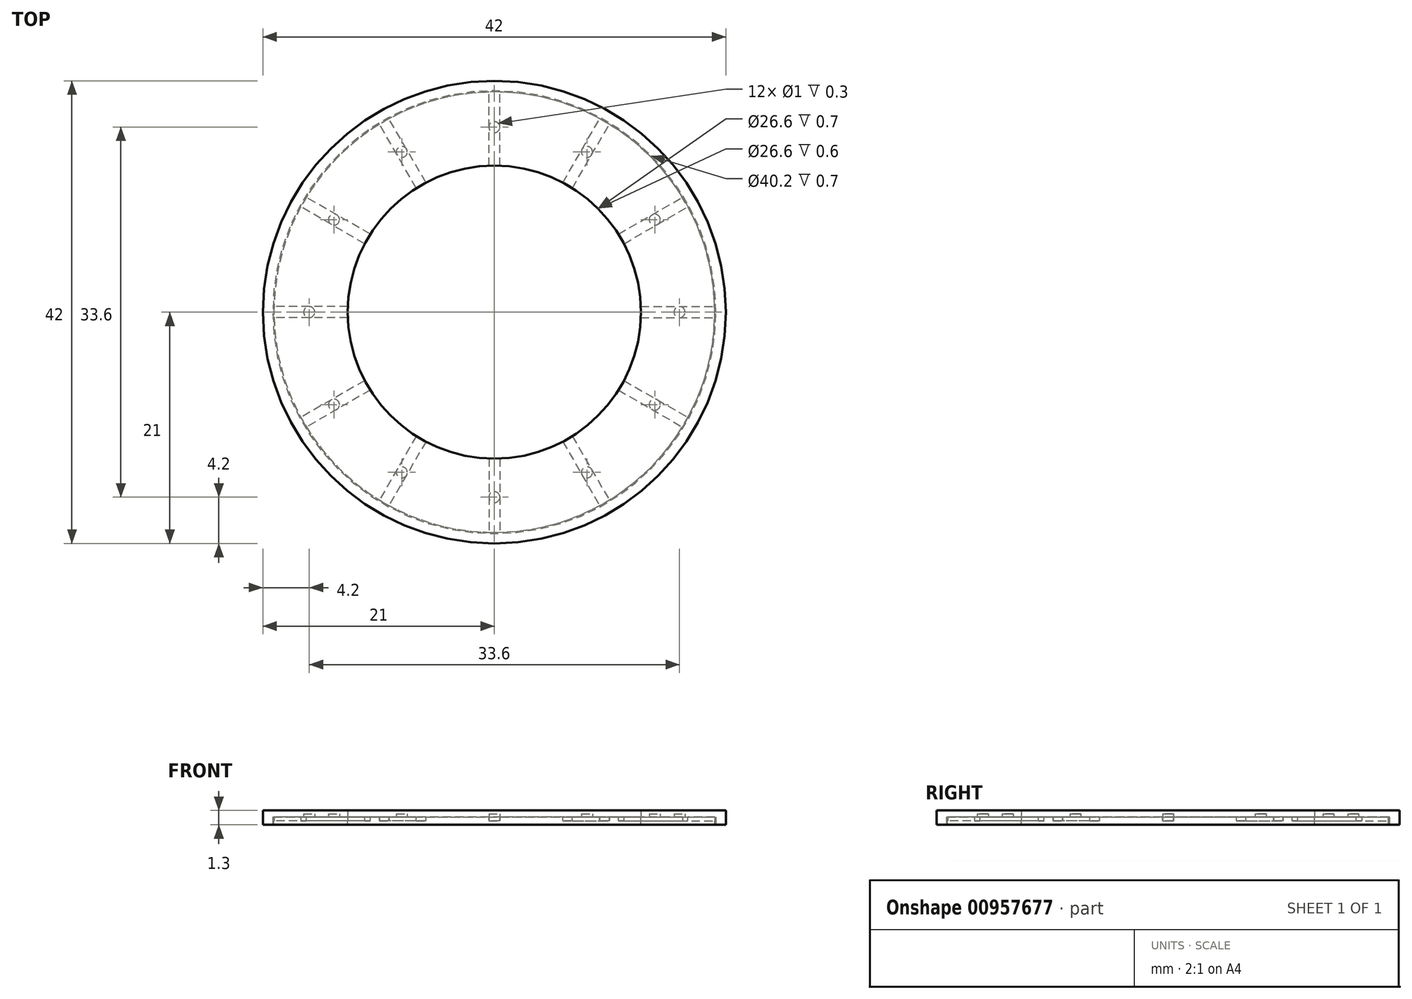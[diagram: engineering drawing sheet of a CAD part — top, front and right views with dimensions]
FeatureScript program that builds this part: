
annotation { "Feature Type Name" : "Feature", "Feature Type Description" : "" }
export const myFeature = defineFeature(function(context is Context, id is Id, definition is map)
    precondition{}
    {
        {
            var Q0;
            Q0=qCreatedBy(makeId("Top.planeOp"),FACE);
            var sketch = newSketch(context, id + "F0", { "sketchPlane" : qUnion([Q0])});
            skCircle(sketch, "E0", {"center": v(0, 0) * mm, "radius": 20 * mm});
            skCircle(sketch, "E1.0", {"center": v(0, 0) * mm, "radius": 13.3 * mm});
            skArc(sketch, "E2", {"start": v(0, 20) * mm, "mid": v(-3.35, 16.65) * mm, "end": v(0, 13.3) * mm});
            skLineSegment(sketch, "E3", {"start": v(0, 13.3) * mm, "end": v(0, 0) * mm, "construction": true});
            skLineSegment(sketch, "E4.1.0", {"start": v(-6.65, 11.52) * mm, "end": v(0, 0) * mm, "construction": true});
            skLineSegment(sketch, "E4.2.0", {"start": v(-11.52, 6.65) * mm, "end": v(0, 0) * mm, "construction": true});
            skLineSegment(sketch, "E5.1.3.0", {"start": v(-13.3, 0) * mm, "end": v(0, 0) * mm, "construction": true});
            skLineSegment(sketch, "E5.1.4.0", {"start": v(-11.52, -6.65) * mm, "end": v(0, 0) * mm, "construction": true});
            skLineSegment(sketch, "E5.1.5.0", {"start": v(-6.65, -11.52) * mm, "end": v(0, 0) * mm, "construction": true});
            skLineSegment(sketch, "E5.1.6.0", {"start": v(0, -13.3) * mm, "end": v(0, 0) * mm, "construction": true});
            skLineSegment(sketch, "E5.1.7.0", {"start": v(6.65, -11.52) * mm, "end": v(0, 0) * mm, "construction": true});
            skLineSegment(sketch, "E5.1.8.0", {"start": v(11.52, -6.65) * mm, "end": v(0, 0) * mm, "construction": true});
            skLineSegment(sketch, "E5.1.9.0", {"start": v(13.3, 0) * mm, "end": v(0, 0) * mm, "construction": true});
            skLineSegment(sketch, "E5.1.10.0", {"start": v(11.52, 6.65) * mm, "end": v(0, 0) * mm, "construction": true});
            skLineSegment(sketch, "E5.1.11.0", {"start": v(6.65, 11.52) * mm, "end": v(0, 0) * mm, "construction": true});
            skLineSegment(sketch, "E6", {"start": v(11.52, -6.65) * mm, "end": v(17.32, -10) * mm, "construction": true});
            skArc(sketch, "E7", {"start": v(17.32, -10) * mm, "mid": v(12.74, -11.23) * mm, "end": v(11.52, -6.65) * mm});
            skCircle(sketch, "E8.0", {"center": v(0, 0) * mm, "radius": 21 * mm});
            skSolve(sketch);
        }
        {
            var Q0;
            {var subQ1=sQuery(id+"F0.wireOp",EDGE,"E2");Q0=makeQuery(id+"F0.imprint","IMPRINT",FACE,{"disambiguationData":[TD([[makeQuery(id+"F0.imprint","IMPRINT",EDGE,{"derivedFrom":subQ1}),1.0]])]});}
            var Q1;
            Q1=makeQuery(id+"F0.imprint","IMPRINT",FACE,{"disambiguationData":[TD([[makeQuery(id+"F0.imprint","IMPRINT",EDGE,{"derivedFrom":sQuery(id+"F0.wireOp",EDGE,"Xude94sI-W2Tp-Iu3P-RemY-LlCTyh9PK2tk")}),1.0]])]});
            var Q2;
            Q2=makeQuery(id+"F0.imprint","IMPRINT",FACE,{"disambiguationData":[TD([[makeQuery(id+"F0.imprint","IMPRINT",EDGE,{"derivedFrom":sQuery(id+"F0.wireOp",EDGE,"zjPRt4QC-Xd3l-se5C-XvQx-mcNvj67eJI4K")}),-1.0]])]});
            extrude(context, id + "F1", {"entities" : qUnion([Q0, Q1, Q2]), "depth" : 0.2 * mm, "offsetDistance" : 25 * mm});
        }
        {
            var Q0;
            Q0=makeQuery(id+"F1.opExtrude","CAP_FACE",FACE,{"disambiguationData":[OSD([sQuery(id+"F0.wireOp",EDGE,"E0"),sQuery(id+"F0.wireOp",EDGE,"E1.0"),sQuery(id+"F0.wireOp",EDGE,"E2"),sQuery(id+"F0.wireOp",EDGE,"E7")])],"isStart":false});
            var sketch = newSketch(context, id + "F2", { "sketchPlane" : qUnion([Q0])});
            skCircle(sketch, "E9", {"center": v(0, 16.65) * mm, "radius": 0.5 * mm});
            skSolve(sketch);
        }
        {
            var Q0;
            Q0=makeQuery(id+"F0.imprint","IMPRINT",FACE,{"disambiguationData":[TD([[makeQuery(id+"F0.imprint","IMPRINT",EDGE,{"derivedFrom":sQuery(id+"F0.wireOp",EDGE,"zjPRt4QC-Xd3l-se5C-XvQx-mcNvj67eJI4K")}),1.0]])]});
            var Q1;
            Q1=makeQuery(id+"F2.imprint","IMPRINT",FACE,{"disambiguationData":[TD([[makeQuery(id+"F2.imprint","IMPRINT",EDGE,{"derivedFrom":sQuery(id+"F2.wireOp",EDGE,"E9")}),1.0]])]});
            extrude(context, id + "F3", {"entities" : qUnion([Q0, Q1]), "operationType" : NewBodyOperationType.ADD, "depth" : 0.3 * mm, "offsetDistance" : 25 * mm});
        }
        {
            var Q0;
            Q0=makeQuery(id+"F1.opExtrude","CAP_FACE",FACE,{"disambiguationData":[OSD([sQuery(id+"F0.wireOp",EDGE,"E0"),sQuery(id+"F0.wireOp",EDGE,"E1.0"),sQuery(id+"F0.wireOp",EDGE,"E2"),sQuery(id+"F0.wireOp",EDGE,"E7")])],"isStart":true});
            var sketch = newSketch(context, id + "F4", { "sketchPlane" : qUnion([Q0])});
            skCircle(sketch, "E10", {"center": v(16.02, 9.25) * mm, "radius": 0.5 * mm});
            skLineSegment(sketch, "E11", {"start": v(11.52, 6.65) * mm, "end": v(17.32, 10) * mm, "construction": true});
            skSolve(sketch);
        }
        {
            var Q0;
            Q0=makeQuery(id+"F4.imprint","IMPRINT",FACE,{"disambiguationData":[TD([[makeQuery(id+"F4.imprint","IMPRINT",EDGE,{"derivedFrom":sQuery(id+"F4.wireOp",EDGE,"E10")}),1.0]])]});
            extrude(context, id + "F5", {"entities" : qUnion([Q0]), "operationType" : NewBodyOperationType.ADD, "depth" : 0.3 * mm, "offsetDistance" : 25 * mm});
        }
        {
            var Q0;
            {var subQ0=sQuery(id+"F0.wireOp",EDGE,"E2");Q0=makeQuery(id+"F0.imprint","IMPRINT",FACE,{"disambiguationData":[TD([[makeQuery(id+"F0.imprint","IMPRINT",EDGE,{"derivedFrom":subQ0}),1.0]])]});}
            var Q1;
            {var subQ0=sQuery(id+"F0.wireOp",EDGE,"E2");Q1=makeQuery(id+"F0.imprint","IMPRINT",FACE,{"disambiguationData":[TD([[makeQuery(id+"F0.imprint","IMPRINT",EDGE,{"derivedFrom":subQ0}),-1.0]])]});}
            extrude(context, id + "F6", {"entities" : qUnion([Q0, Q1]), "depth" : 0.6 * mm, "offsetDistance" : 25 * mm});
        }
        {
            var Q0;
            Q0=makeQuery(id+"F0.imprint","IMPRINT",FACE,{"disambiguationData":[TD([[makeQuery(id+"F0.imprint","IMPRINT",EDGE,{"derivedFrom":sQuery(id+"F0.wireOp",EDGE,"E8.0")}),1.0]])]});
            var Q1;
            Q1=sQuery(id+"F0.wireOp",EDGE,"E8.0");
            var Q2;
            Q2=makeQuery(id+"F6.opExtrude","CAP_FACE",FACE,{"disambiguationData":[OSD([sQuery(id+"F0.wireOp",EDGE,"E0"),sQuery(id+"F0.wireOp",EDGE,"E1.0")])],"isStart":false});
            extrude(context, id + "F7", {"entities" : qUnion([Q0]), "operationType" : NewBodyOperationType.ADD, "surfaceEntities" : qUnion([Q1]), "endBound" : BoundingType.UP_TO_SURFACE, "depth" : 25 * mm, "endBoundEntityFace" : qUnion([Q2]), "offsetDistance" : 25 * mm, "hasSecondDirection" : true, "secondDirectionOppositeDirection" : true, "secondDirectionDepth" : 0.7 * mm});
        }
        {
            var Q0;
            Q0=makeQuery(id+"F7.opExtrude","CAP_FACE",FACE,{"disambiguationData":[OSD([sQuery(id+"F0.wireOp",EDGE,"E0"),sQuery(id+"F0.wireOp",EDGE,"E8.0")])],"isStart":true});
            var sketch = newSketch(context, id + "F8", { "sketchPlane" : qUnion([Q0])});
            skCircle(sketch, "E12.0", {"center": v(0, 0) * mm, "radius": 20.1 * mm});
            skSolve(sketch);
        }
        {
            var Q0;
            Q0 = qSketchRegion(id + "F8", true);
            extrude(context, id + "F9", {"entities" : qUnion([Q0]), "operationType" : NewBodyOperationType.REMOVE, "oppositeDirection" : true, "depth" : 0.7 * mm, "offsetDistance" : 25 * mm});
        }
        {
            var Q0;
            Q0=makeQuery(id+"F6.opExtrude","CAP_FACE",FACE,{"disambiguationData":[OSD([sQuery(id+"F0.wireOp",EDGE,"E0"),sQuery(id+"F0.wireOp",EDGE,"E1.0")])],"isStart":true});
            var sketch = newSketch(context, id + "F10", { "sketchPlane" : qUnion([Q0])});
            skLineSegment(sketch, "E13", {"start": v(0, -20.3) * mm, "end": v(0, -13.3) * mm, "construction": true});
            skCircle(sketch, "E14", {"center": v(0, -16.8) * mm, "radius": 0.5 * mm});
            skCircle(sketch, "E15.1.0", {"center": v(8.4, -14.55) * mm, "radius": 0.5 * mm});
            skCircle(sketch, "E15.2.0", {"center": v(14.55, -8.4) * mm, "radius": 0.5 * mm});
            skCircle(sketch, "E15.3.0", {"center": v(16.8, 0) * mm, "radius": 0.5 * mm});
            skCircle(sketch, "E15.4.0", {"center": v(14.55, 8.4) * mm, "radius": 0.5 * mm});
            skCircle(sketch, "E15.5.0", {"center": v(8.4, 14.55) * mm, "radius": 0.5 * mm});
            skCircle(sketch, "E15.6.0", {"center": v(0, 16.8) * mm, "radius": 0.5 * mm});
            skCircle(sketch, "E15.7.0", {"center": v(-8.4, 14.55) * mm, "radius": 0.5 * mm});
            skCircle(sketch, "E15.8.0", {"center": v(-14.55, 8.4) * mm, "radius": 0.5 * mm});
            skCircle(sketch, "E15.9.0", {"center": v(-16.8, 0) * mm, "radius": 0.5 * mm});
            skCircle(sketch, "E15.10.0", {"center": v(-14.55, -8.4) * mm, "radius": 0.5 * mm});
            skCircle(sketch, "E15.11.0", {"center": v(-8.4, -14.55) * mm, "radius": 0.5 * mm});
            skPoint(sketch, "E15.center", {"position": v(0, 0) * mm});
            skSolve(sketch);
        }
        {
            var Q0;
            Q0 = qSketchRegion(id + "F10", true);
            extrude(context, id + "F11", {"entities" : qUnion([Q0]), "operationType" : NewBodyOperationType.REMOVE, "oppositeDirection" : true, "depth" : 0.3 * mm, "offsetDistance" : 25 * mm});
        }
        {
            var Q0;
            {var subQ0=sQuery(id+"F0.wireOp",EDGE,"E2");Q0=makeQuery(id+"F0.imprint","IMPRINT",FACE,{"disambiguationData":[TD([[makeQuery(id+"F0.imprint","IMPRINT",EDGE,{"derivedFrom":subQ0}),-1.0]])]});}
            var Q1;
            {var subQ0=sQuery(id+"F0.wireOp",EDGE,"E2");Q1=makeQuery(id+"F0.imprint","IMPRINT",FACE,{"disambiguationData":[TD([[makeQuery(id+"F0.imprint","IMPRINT",EDGE,{"derivedFrom":subQ0}),1.0]])]});}
            var Q2;
            Q2=makeQuery(id+"F0.imprint","IMPRINT",FACE,{"disambiguationData":[TD([[makeQuery(id+"F0.imprint","IMPRINT",EDGE,{"derivedFrom":sQuery(id+"F0.wireOp",EDGE,"5PKALqbX-9KFI-Jdac-h9Fq-azR43dOAAVFC")}),1.0]])]});
            var Q3;
            Q3=makeQuery(id+"F0.imprint","IMPRINT",FACE,{"disambiguationData":[TD([[makeQuery(id+"F0.imprint","IMPRINT",EDGE,{"derivedFrom":sQuery(id+"F0.wireOp",EDGE,"AgC7d66J-9GNQ-Cd2n-w5tn-KuAWBY92KT90")}),1.0]])]});
            var Q4;
            Q4=makeQuery(id+"F0.imprint","IMPRINT",FACE,{"disambiguationData":[TD([[makeQuery(id+"F0.imprint","IMPRINT",EDGE,{"derivedFrom":sQuery(id+"F0.wireOp",EDGE,"Xude94sI-W2Tp-Iu3P-RemY-LlCTyh9PK2tk")}),1.0]])]});
            var Q5;
            Q5=makeQuery(id+"F0.imprint","IMPRINT",FACE,{"disambiguationData":[TD([[makeQuery(id+"F0.imprint","IMPRINT",EDGE,{"derivedFrom":sQuery(id+"F0.wireOp",EDGE,"G0UDFLS0-c3lv-gHoS-E3xn-spBDKPuhMolK")}),1.0]])]});
            var Q6;
            Q6=makeQuery(id+"F0.imprint","IMPRINT",FACE,{"disambiguationData":[TD([[makeQuery(id+"F0.imprint","IMPRINT",EDGE,{"derivedFrom":sQuery(id+"F0.wireOp",EDGE,"S2n5unBn-GXa3-67Jl-It38-8oYZM1jEPxRn")}),1.0]])]});
            var Q7;
            {var subQ5=sQuery(id+"F0.wireOp",EDGE,"7f034801-caaf-4e82-90cd-c4149f58e414.0.startCap");Q7=makeQuery(id+"F0.imprint","IMPRINT",FACE,{"disambiguationData":[TD([[makeQuery(id+"F0.imprint","IMPRINT",EDGE,{"derivedFrom":subQ5}),-1.0]])]});}
            var Q8;
            Q8=makeQuery(id+"F0.imprint","IMPRINT",FACE,{"disambiguationData":[TD([[makeQuery(id+"F0.imprint","IMPRINT",EDGE,{"derivedFrom":sQuery(id+"F0.wireOp",EDGE,"zjPRt4QC-Xd3l-se5C-XvQx-mcNvj67eJI4K")}),-1.0]])]});
            var Q9;
            Q9=makeQuery(id+"F0.imprint","IMPRINT",FACE,{"disambiguationData":[TD([[makeQuery(id+"F0.imprint","IMPRINT",EDGE,{"derivedFrom":sQuery(id+"F0.wireOp",EDGE,"zjPRt4QC-Xd3l-se5C-XvQx-mcNvj67eJI4K")}),1.0]])]});
            extrude(context, id + "F12", {"entities" : qUnion([Q0, Q1, Q2, Q3, Q4, Q5, Q6, Q7, Q8, Q9]), "oppositeDirection" : true, "depth" : 0.7 * mm, "offsetDistance" : 25 * mm});
        }
        {
            var Q0;
            Q0=makeQuery(id+"F12.opExtrude","CAP_FACE",FACE,{"disambiguationData":[OSD([sQuery(id+"F0.wireOp",EDGE,"E0"),sQuery(id+"F0.wireOp",EDGE,"E1.0")])],"isStart":true});
            var sketch = newSketch(context, id + "F13", { "sketchPlane" : qUnion([Q0])});
            skCircle(sketch, "E16", {"center": v(0, 0) * mm, "radius": 20 * mm});
            skCircle(sketch, "E17.0", {"center": v(0, 0) * mm, "radius": 13 * mm});
            skLineSegment(sketch, "E18", {"start": v(0, 13) * mm, "end": v(0, 0) * mm, "construction": true});
            skLineSegment(sketch, "E19.1.0", {"start": v(-6.5, 11.26) * mm, "end": v(0, 0) * mm, "construction": true});
            skLineSegment(sketch, "E19.2.0", {"start": v(-11.26, 6.5) * mm, "end": v(0, 0) * mm, "construction": true});
            skLineSegment(sketch, "E20.1.3.0", {"start": v(-13, 0) * mm, "end": v(0, 0) * mm, "construction": true});
            skLineSegment(sketch, "E20.1.4.0", {"start": v(-11.26, -6.5) * mm, "end": v(0, 0) * mm, "construction": true});
            skLineSegment(sketch, "E20.1.5.0", {"start": v(-6.5, -11.26) * mm, "end": v(0, 0) * mm, "construction": true});
            skLineSegment(sketch, "E20.1.6.0", {"start": v(0, -13) * mm, "end": v(0, 0) * mm, "construction": true});
            skLineSegment(sketch, "E20.1.7.0", {"start": v(6.5, -11.26) * mm, "end": v(0, 0) * mm, "construction": true});
            skLineSegment(sketch, "E20.1.8.0", {"start": v(11.26, -6.5) * mm, "end": v(0, 0) * mm, "construction": true});
            skLineSegment(sketch, "E20.1.9.0", {"start": v(13, 0) * mm, "end": v(0, 0) * mm, "construction": true});
            skLineSegment(sketch, "E20.1.10.0", {"start": v(11.26, 6.5) * mm, "end": v(0, 0) * mm, "construction": true});
            skLineSegment(sketch, "E20.1.11.0", {"start": v(6.5, 11.26) * mm, "end": v(0, 0) * mm, "construction": true});
            skLineSegment(sketch, "E21", {"start": v(11.26, -6.5) * mm, "end": v(17.32, -10) * mm, "construction": true});
            skLineSegment(sketch, "E22", {"start": v(11.76, -6.21) * mm, "end": v(17.57, -9.56) * mm});
            skLineSegment(sketch, "E23", {"start": v(11.26, -7.08) * mm, "end": v(17.07, -10.43) * mm});
            skLineSegment(sketch, "E24.1.0", {"start": v(13.3, -0.5) * mm, "end": v(20, -0.5) * mm});
            skLineSegment(sketch, "E24.1.1", {"start": v(13.3, 0.5) * mm, "end": v(20, 0.5) * mm});
            skLineSegment(sketch, "E24.2.0", {"start": v(11.76, 6.21) * mm, "end": v(17.57, 9.56) * mm});
            skLineSegment(sketch, "E24.2.1", {"start": v(11.26, 7.08) * mm, "end": v(17.07, 10.43) * mm});
            skLineSegment(sketch, "E24.3.0", {"start": v(7.08, 11.26) * mm, "end": v(10.43, 17.07) * mm});
            skLineSegment(sketch, "E24.3.1", {"start": v(6.21, 11.76) * mm, "end": v(9.56, 17.57) * mm});
            skLineSegment(sketch, "E24.4.0", {"start": v(0.5, 13.3) * mm, "end": v(0.5, 20) * mm});
            skLineSegment(sketch, "E24.4.1", {"start": v(-0.5, 13.3) * mm, "end": v(-0.5, 20) * mm});
            skLineSegment(sketch, "E24.5.0", {"start": v(-6.21, 11.76) * mm, "end": v(-9.56, 17.57) * mm});
            skLineSegment(sketch, "E24.5.1", {"start": v(-7.08, 11.26) * mm, "end": v(-10.43, 17.07) * mm});
            skLineSegment(sketch, "E24.6.0", {"start": v(-11.26, 7.08) * mm, "end": v(-17.07, 10.43) * mm});
            skLineSegment(sketch, "E24.6.1", {"start": v(-11.76, 6.21) * mm, "end": v(-17.57, 9.56) * mm});
            skLineSegment(sketch, "E24.7.0", {"start": v(-13.3, 0.5) * mm, "end": v(-20, 0.5) * mm});
            skLineSegment(sketch, "E24.7.1", {"start": v(-13.3, -0.5) * mm, "end": v(-20, -0.5) * mm});
            skLineSegment(sketch, "E24.8.0", {"start": v(-11.76, -6.21) * mm, "end": v(-17.57, -9.56) * mm});
            skLineSegment(sketch, "E24.8.1", {"start": v(-11.26, -7.08) * mm, "end": v(-17.07, -10.43) * mm});
            skLineSegment(sketch, "E24.9.0", {"start": v(-7.08, -11.26) * mm, "end": v(-10.43, -17.07) * mm});
            skLineSegment(sketch, "E24.9.1", {"start": v(-6.21, -11.76) * mm, "end": v(-9.56, -17.57) * mm});
            skLineSegment(sketch, "E24.10.0", {"start": v(-0.5, -13.3) * mm, "end": v(-0.5, -20) * mm});
            skLineSegment(sketch, "E24.10.1", {"start": v(0.5, -13.3) * mm, "end": v(0.5, -20) * mm});
            skLineSegment(sketch, "E24.11.0", {"start": v(6.21, -11.76) * mm, "end": v(9.56, -17.57) * mm});
            skLineSegment(sketch, "E24.11.1", {"start": v(7.08, -11.26) * mm, "end": v(10.43, -17.07) * mm});
            skSolve(sketch);
        }
        {
            var Q0;
            {var subQ0=sQuery(id+"F13.wireOp",EDGE,"E24.2.0");Q0=makeQuery(id+"F13.imprint","IMPRINT",FACE,{"disambiguationData":[TD([[makeQuery(id+"F13.imprint","IMPRINT",EDGE,{"derivedFrom":subQ0}),1.0]])]});}
            var Q1;
            {var subQ0=sQuery(id+"F13.wireOp",EDGE,"E24.3.0");Q1=makeQuery(id+"F13.imprint","IMPRINT",FACE,{"disambiguationData":[TD([[makeQuery(id+"F13.imprint","IMPRINT",EDGE,{"derivedFrom":subQ0}),1.0]])]});}
            var Q2;
            {var subQ0=sQuery(id+"F13.wireOp",EDGE,"E24.4.0");Q2=makeQuery(id+"F13.imprint","IMPRINT",FACE,{"disambiguationData":[TD([[makeQuery(id+"F13.imprint","IMPRINT",EDGE,{"derivedFrom":subQ0}),1.0]])]});}
            var Q3;
            {var subQ0=sQuery(id+"F13.wireOp",EDGE,"E24.5.0");Q3=makeQuery(id+"F13.imprint","IMPRINT",FACE,{"disambiguationData":[TD([[makeQuery(id+"F13.imprint","IMPRINT",EDGE,{"derivedFrom":subQ0}),1.0]])]});}
            var Q4;
            {var subQ0=sQuery(id+"F13.wireOp",EDGE,"E24.6.0");Q4=makeQuery(id+"F13.imprint","IMPRINT",FACE,{"disambiguationData":[TD([[makeQuery(id+"F13.imprint","IMPRINT",EDGE,{"derivedFrom":subQ0}),1.0]])]});}
            var Q5;
            {var subQ0=sQuery(id+"F13.wireOp",EDGE,"E24.7.0");Q5=makeQuery(id+"F13.imprint","IMPRINT",FACE,{"disambiguationData":[TD([[makeQuery(id+"F13.imprint","IMPRINT",EDGE,{"derivedFrom":subQ0}),1.0]])]});}
            var Q6;
            {var subQ0=sQuery(id+"F13.wireOp",EDGE,"E24.8.0");Q6=makeQuery(id+"F13.imprint","IMPRINT",FACE,{"disambiguationData":[TD([[makeQuery(id+"F13.imprint","IMPRINT",EDGE,{"derivedFrom":subQ0}),1.0]])]});}
            var Q7;
            {var subQ0=sQuery(id+"F13.wireOp",EDGE,"E24.9.0");Q7=makeQuery(id+"F13.imprint","IMPRINT",FACE,{"disambiguationData":[TD([[makeQuery(id+"F13.imprint","IMPRINT",EDGE,{"derivedFrom":subQ0}),1.0]])]});}
            var Q8;
            {var subQ0=sQuery(id+"F13.wireOp",EDGE,"E22");Q8=makeQuery(id+"F13.imprint","IMPRINT",FACE,{"disambiguationData":[TD([[makeQuery(id+"F13.imprint","IMPRINT",EDGE,{"derivedFrom":subQ0}),-1.0]])]});}
            var Q9;
            {var subQ0=sQuery(id+"F13.wireOp",EDGE,"E24.1.0");Q9=makeQuery(id+"F13.imprint","IMPRINT",FACE,{"disambiguationData":[TD([[makeQuery(id+"F13.imprint","IMPRINT",EDGE,{"derivedFrom":subQ0}),1.0]])]});}
            var Q10;
            {var subQ0=sQuery(id+"F13.wireOp",EDGE,"E24.10.0");Q10=makeQuery(id+"F13.imprint","IMPRINT",FACE,{"disambiguationData":[TD([[makeQuery(id+"F13.imprint","IMPRINT",EDGE,{"derivedFrom":subQ0}),1.0]])]});}
            var Q11;
            {var subQ0=sQuery(id+"F13.wireOp",EDGE,"E24.11.0");Q11=makeQuery(id+"F13.imprint","IMPRINT",FACE,{"disambiguationData":[TD([[makeQuery(id+"F13.imprint","IMPRINT",EDGE,{"derivedFrom":subQ0}),1.0]])]});}
            extrude(context, id + "F14", {"entities" : qUnion([Q0, Q1, Q2, Q3, Q4, Q5, Q6, Q7, Q8, Q9, Q10, Q11]), "operationType" : NewBodyOperationType.REMOVE, "oppositeDirection" : true, "depth" : 0.35 * mm, "offsetDistance" : 25 * mm});
        }
    });
